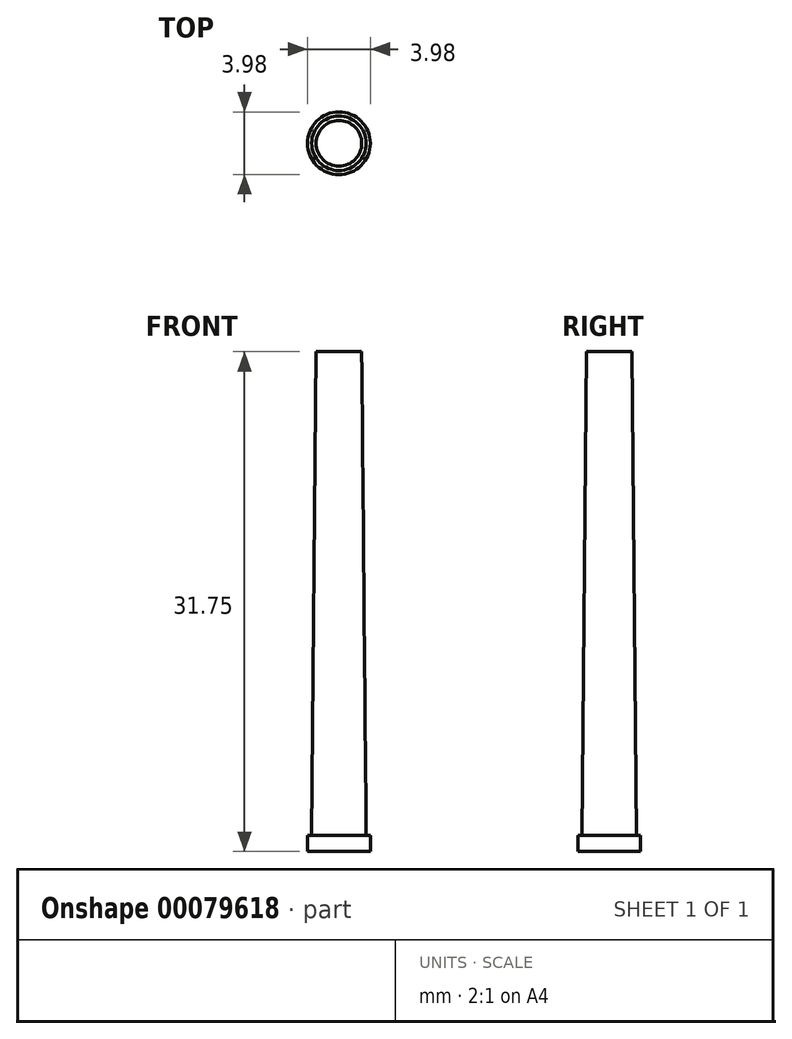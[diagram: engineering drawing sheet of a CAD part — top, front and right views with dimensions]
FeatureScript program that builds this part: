
annotation { "Feature Type Name" : "Feature", "Feature Type Description" : "" }
export const myFeature = defineFeature(function(context is Context, id is Id, definition is map)
    precondition{}
    {
        {
            var Q0;
            Q0=qCreatedBy(makeId("Top.planeOp"),FACE);
            var sketch = newSketch(context, id + "F0", { "sketchPlane" : qUnion([Q0])});
            skCircle(sketch, "E0", {"center": v(0, 0) * mm, "radius": 1.74 * mm});
            skSolve(sketch);
        }
        {
            var Q0;
            Q0=qCreatedBy(makeId("Top.planeOp"),FACE);
            cPlane(context, id + "F1", {"entities" : qUnion([Q0]), "cplaneType" : CPlaneType.OFFSET, "offset" : 31.75 * mm, "width" : 152.4 * mm, "height" : 152.4 * mm});
        }
        {
            var Q0;
            Q0=qCreatedBy(id+"F1.planeOp",FACE);
            var sketch = newSketch(context, id + "F2", { "sketchPlane" : qUnion([Q0])});
            skCircle(sketch, "E1", {"center": v(0, 0) * mm, "radius": 1.45 * mm});
            skSolve(sketch);
        }
        {
            var Q0;
            Q0 = qSketchRegion(id + "F0", true);
            var Q1;
            Q1 = qSketchRegion(id + "F2", true);
            loft(context, id + "F3", {"sheetProfilesArray" : [{ "sheetProfileEntities" : qUnion([Q0]) }, { "sheetProfileEntities" : qUnion([Q1]) }]});
        }
        {
            var Q0;
            Q0=qCreatedBy(makeId("Top.planeOp"),FACE);
            var sketch = newSketch(context, id + "F4", { "sketchPlane" : qUnion([Q0])});
            skCircle(sketch, "E2", {"center": v(0, 0) * mm, "radius": 2 * mm});
            skSolve(sketch);
        }
        {
            var Q0;
            Q0 = qSketchRegion(id + "F4", true);
            extrude(context, id + "F5", {"entities" : qUnion([Q0]), "operationType" : NewBodyOperationType.ADD, "depth" : 1.02 * mm});
        }
    });
